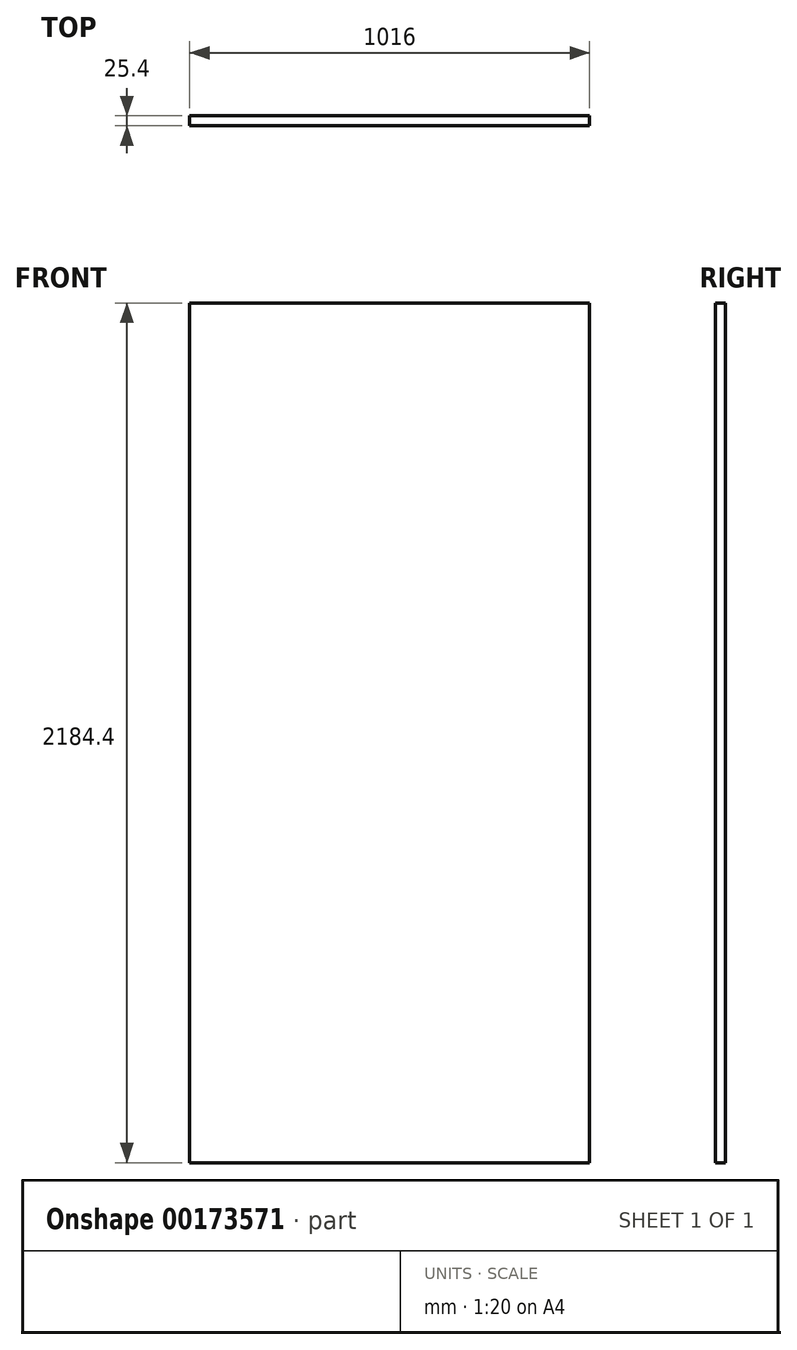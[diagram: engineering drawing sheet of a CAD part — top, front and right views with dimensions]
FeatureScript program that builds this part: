
annotation { "Feature Type Name" : "Feature", "Feature Type Description" : "" }
export const myFeature = defineFeature(function(context is Context, id is Id, definition is map)
    precondition{}
    {
        {
            var Q0;
            Q0=qCreatedBy(makeId("Front.planeOp"),FACE);
            var sketch = newSketch(context, id + "F0", { "sketchPlane" : qUnion([Q0])});
            skLineSegment(sketch, "E0.bottom", {"start": v(508, 1092.2) * mm, "end": v(-508, 1092.2) * mm});
            skLineSegment(sketch, "E0.top", {"start": v(508, -1092.2) * mm, "end": v(-508, -1092.2) * mm});
            skLineSegment(sketch, "E0.left", {"start": v(508, 1092.2) * mm, "end": v(508, -1092.2) * mm});
            skLineSegment(sketch, "E0.right", {"start": v(-508, 1092.2) * mm, "end": v(-508, -1092.2) * mm});
            skPoint(sketch, "E0.middle", {"position": v(0, 0) * mm});
            skSolve(sketch);
        }
        {
            var Q0;
            Q0 = qSketchRegion(id + "F0", true);
            extrude(context, id + "F1", {"entities" : qUnion([Q0]), "depth" : 25.4 * mm});
        }
    });
